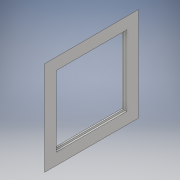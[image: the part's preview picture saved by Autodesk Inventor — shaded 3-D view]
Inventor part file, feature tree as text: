
AUTODESK INVENTOR PART (.ipt)
format: ipt  version: 2018.3 (Build 223284000, 284)  size: 156,160 bytes
history: native  units: mm
features: reference x21, extrude x4, sketch x4, projected_geometry x3, other x3, chamfer x2
ambient origin geometry x8: Origin, YZ Plane, XZ Plane, XY Plane, X Axis, Y Axis, Z Axis, Center Point
bodies: Volumenkörper1 (feature_tree)
feature tree (37):
  extrude  "Extrusion1"  Depth=540.0mm
  extrude  "Extrusion2"  Depth=67.0mm
  extrude  "Extrusion3"  Depth=67.0mm
  sketch  "Skizze6"  dims[d7=67.0mm d8=10.0mm d9=0.0mm d10=10.0mm d11=10.0mm d12=10.0mm d13=10.0mm d14=8.0mm d15=0.0mm d26=18.0mm d27=2.0mm d28=45.0deg d31=18.0mm d32=2.0mm d33=45.0deg d34=50.0mm d37=50.0mm d38=15.0mm d39=0.0mm]
  chamfer  "Fase1"  Distance=10.0mm
  chamfer  "Fase2"  Distance=10.0mm
  extrude  "Extrusion7"  Depth=10.0mm
  sketch  "Skizze1"  dims[d0=540.0mm d1=540.0mm]
  sketch  "Skizze2"  dims[d2=18.0mm d3=0.0mm d4=67.0mm]
  projected_geometry  "Projizierte Kontur1"
  sketch  "Skizze3"  dims[d5=67.0mm d6=67.0mm]
  projected_geometry  "Projizierte Kontur2"
  projected_geometry  "Projizierte Kontur4"
  reference  "Referenz29"
  reference  "Referenz30"
  reference  "Referenz31"
  reference  "Referenz32"
  reference  "Referenz33"
  reference  "Referenz34"
  reference  "Referenz35"
  reference  "Referenz36"
  reference  "Referenz37"
  reference  "Referenz38"
  reference  "Referenz39"
  reference  "Referenz40"
  reference  "Referenz41"
  reference  "Referenz42"
  reference  "Referenz43"
  reference  "Referenz44"
  reference  "Referenz45"
  reference  "Referenz46"
  reference  "Referenz47"
  reference  "Referenz48"
  reference  "Referenz49"
  parser-record x1  (decoder bookkeeping rows leaked as tree rows — omitted from the tree; the rows remain in map.json)
  other  "Baugruppe1.iam"
  other  "PV_Modul_CPY_3:1"
note: 1 file-system path scrubbed to <path> (originals preserved in map.json)
